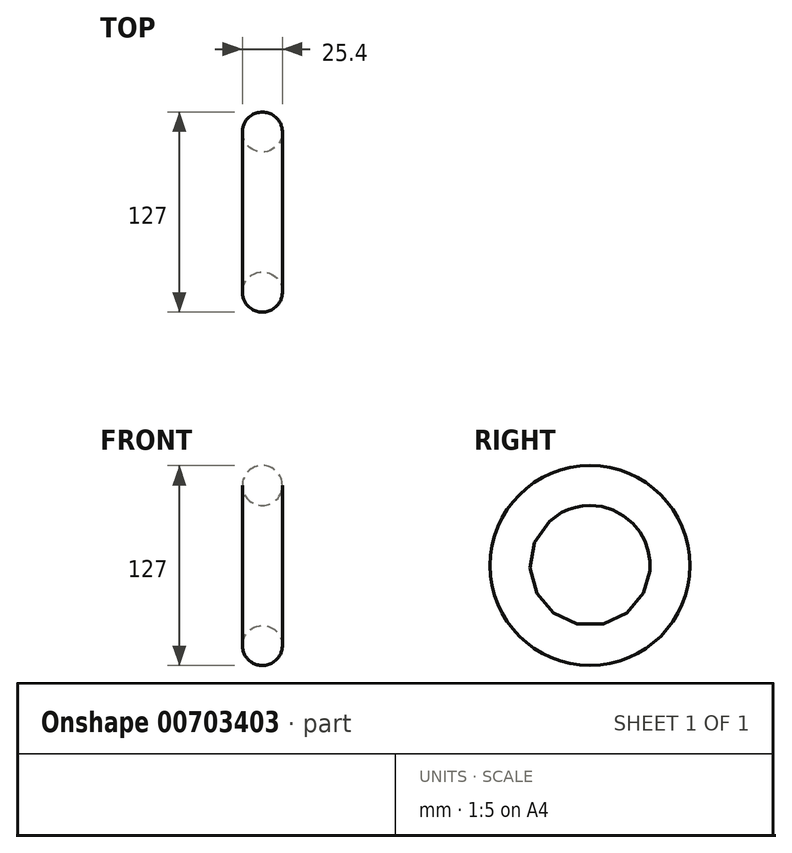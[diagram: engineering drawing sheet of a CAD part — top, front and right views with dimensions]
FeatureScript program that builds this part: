
annotation { "Feature Type Name" : "Feature", "Feature Type Description" : "" }
export const myFeature = defineFeature(function(context is Context, id is Id, definition is map)
    precondition{}
    {
        {
            var Q0;
            Q0=qCreatedBy(makeId("Top.planeOp"),FACE);
            var sketch = newSketch(context, id + "F0", { "sketchPlane" : qUnion([Q0])});
            skCircle(sketch, "E0", {"center": v(0, 50.8) * mm, "radius": 12.7 * mm});
            skLineSegment(sketch, "E1", {"start": v(-41.75, 0) * mm, "end": v(40.59, 0) * mm});
            skSolve(sketch);
        }
        {
            var Q0;
            Q0=makeQuery(id+"F0.imprint","IMPRINT",FACE,{"disambiguationData":[TD([[makeQuery(id+"F0.imprint","IMPRINT",EDGE,{"derivedFrom":sQuery(id+"F0.wireOp",EDGE,"E0")}),1.0]])]});
            var Q1;
            Q1=sQuery(id+"F0.wireOp",EDGE,"E1");
            revolve(context, id + "F1", {"surfaceOperationType" : NewSurfaceOperationType.NEW, "entities" : qUnion([Q0]), "axis" : qUnion([Q1]), "revolveType" : RevolveType.FULL});
        }
    });
